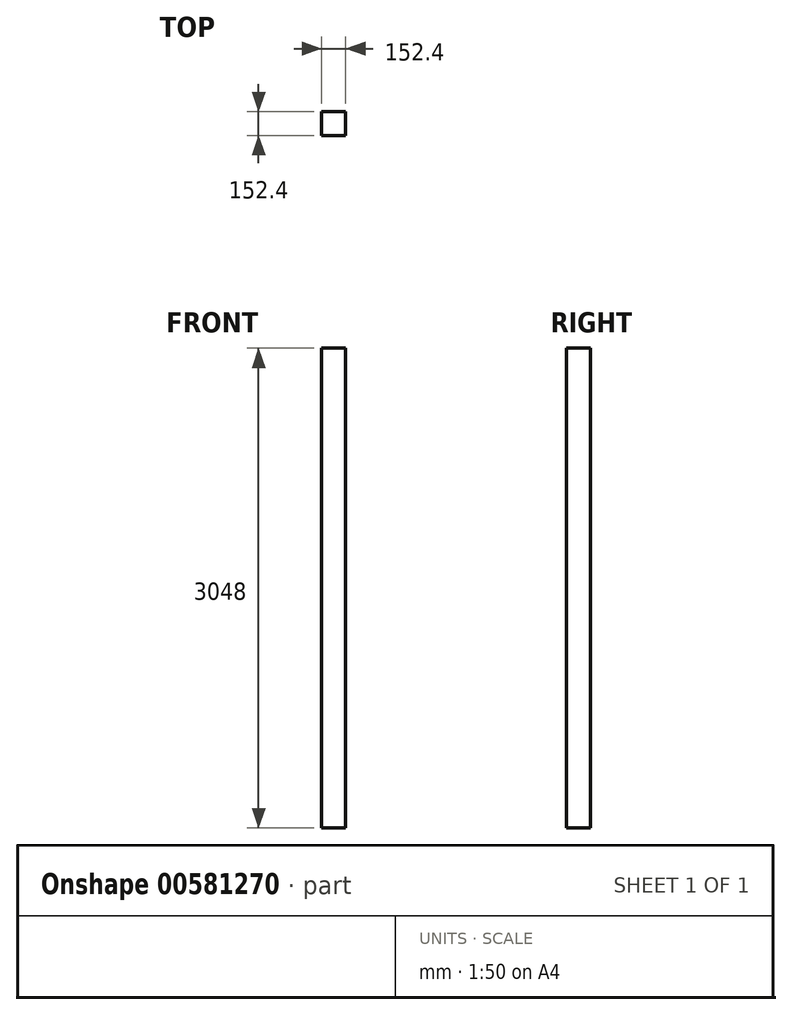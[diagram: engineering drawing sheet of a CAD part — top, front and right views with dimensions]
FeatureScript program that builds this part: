
annotation { "Feature Type Name" : "Feature", "Feature Type Description" : "" }
export const myFeature = defineFeature(function(context is Context, id is Id, definition is map)
    precondition{}
    {
        {
            var Q0;
            Q0=qCreatedBy(makeId("Front.planeOp"),FACE);
            var sketch = newSketch(context, id + "F0", { "sketchPlane" : qUnion([Q0])});
            skLineSegment(sketch, "E0.bottom", {"start": v(-170.83, 0) * mm, "end": v(-18.43, 0) * mm});
            skLineSegment(sketch, "E0.top", {"start": v(-170.83, 3048) * mm, "end": v(-18.43, 3048) * mm});
            skLineSegment(sketch, "E0.left", {"start": v(-170.83, 0) * mm, "end": v(-170.83, 3048) * mm});
            skLineSegment(sketch, "E0.right", {"start": v(-18.43, 0) * mm, "end": v(-18.43, 3048) * mm});
            skSolve(sketch);
        }
        {
            var Q0;
            Q0=makeQuery(id+"F0.imprint","IMPRINT",FACE,{"disambiguationData":[TD([[makeQuery(id+"F0.imprint","IMPRINT",EDGE,{"derivedFrom":sQuery(id+"F0.wireOp",EDGE,"E0.bottom")}),1.0]])]});
            extrude(context, id + "F1", {"entities" : qUnion([Q0]), "endBound" : BoundingType.SYMMETRIC, "depth" : 152.4 * mm, "offsetDistance" : 25.4 * mm});
        }
    });
